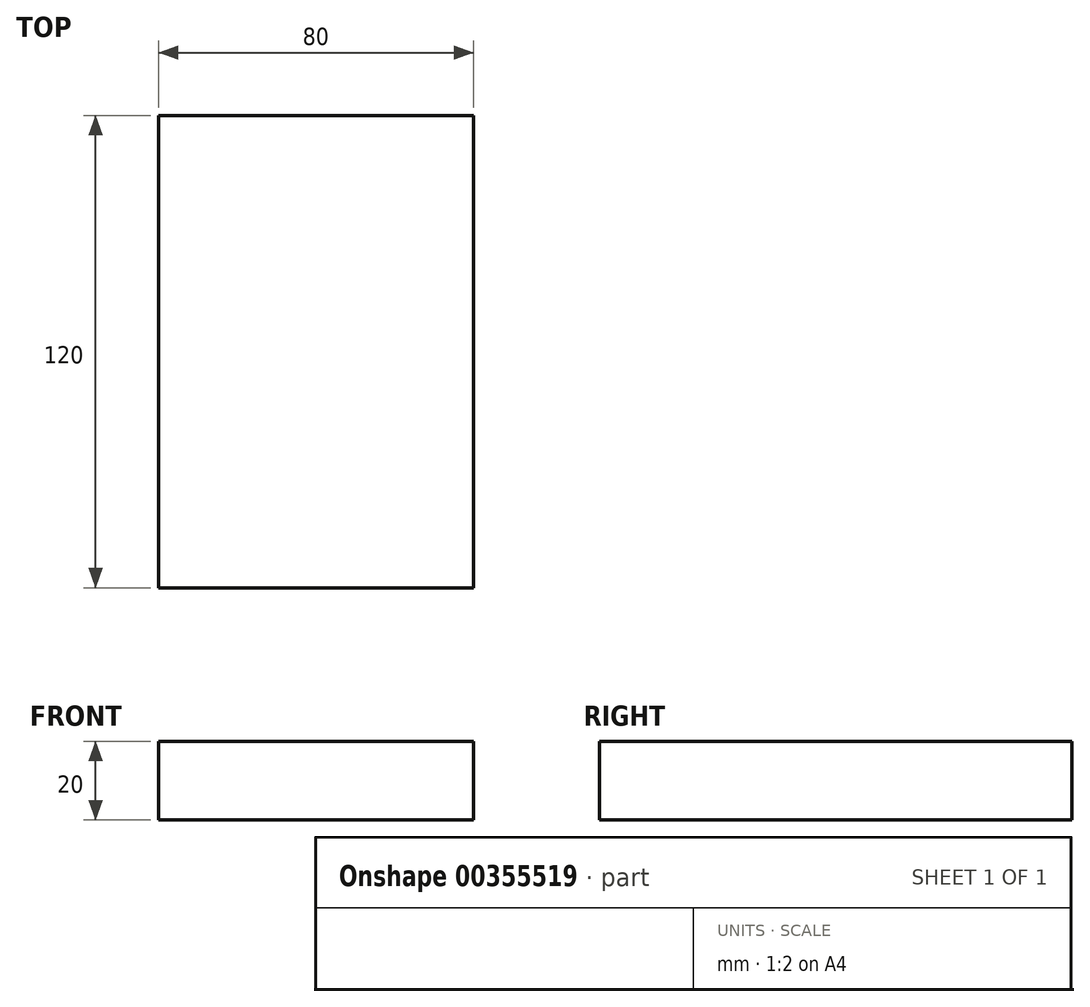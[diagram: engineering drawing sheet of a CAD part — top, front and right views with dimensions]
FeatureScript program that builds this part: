
annotation { "Feature Type Name" : "Feature", "Feature Type Description" : "" }
export const myFeature = defineFeature(function(context is Context, id is Id, definition is map)
    precondition{}
    {
        {
            var Q0;
            Q0=qCreatedBy(makeId("Front.planeOp"),FACE);
            var sketch = newSketch(context, id + "F0", { "sketchPlane" : qUnion([Q0])});
            skLineSegment(sketch, "E0.bottom", {"start": v(40, 10) * mm, "end": v(-40, 10) * mm});
            skLineSegment(sketch, "E0.top", {"start": v(40, -10) * mm, "end": v(-40, -10) * mm});
            skLineSegment(sketch, "E0.left", {"start": v(40, 10) * mm, "end": v(40, -10) * mm});
            skLineSegment(sketch, "E0.right", {"start": v(-40, 10) * mm, "end": v(-40, -10) * mm});
            skPoint(sketch, "E0.middle", {"position": v(0, 0) * mm});
            skLineSegment(sketch, "E1.bottom", {"start": v(110, 70) * mm, "end": v(60, 70) * mm});
            skLineSegment(sketch, "E1.top", {"start": v(110, 40) * mm, "end": v(60, 40) * mm});
            skLineSegment(sketch, "E1.left", {"start": v(110, 70) * mm, "end": v(110, 40) * mm});
            skLineSegment(sketch, "E1.right", {"start": v(60, 70) * mm, "end": v(60, 40) * mm});
            skPoint(sketch, "E1.middle", {"position": v(85, 55) * mm});
            skLineSegment(sketch, "E2", {"start": v(40, 10) * mm, "end": v(40, 38.08) * mm});
            skArc(sketch, "E3", {"start": v(40, 38.08) * mm, "mid": v(43.51, 46.57) * mm, "end": v(52, 50.08) * mm});
            skLineSegment(sketch, "E4", {"start": v(52, 50.08) * mm, "end": v(85, 50.08) * mm});
            skLineSegment(sketch, "E5.0", {"start": v(52, 62.08) * mm, "end": v(85, 62.08) * mm});
            skArc(sketch, "E5.1", {"start": v(28, 38.08) * mm, "mid": v(35.03, 55.05) * mm, "end": v(52, 62.08) * mm});
            skLineSegment(sketch, "E5.2", {"start": v(28, 10) * mm, "end": v(28, 38.08) * mm});
            skLineSegment(sketch, "E6", {"start": v(85, 70) * mm, "end": v(85, 40) * mm});
            skFitSpline(sketch, "E7", {"points": [v(-40, 10) * mm, v(52, 62.08) * mm], "startDerivative": vector(13.37, 56.52) * mm, "endDerivative": vector(129.8, 3.37) * mm});
            skSolve(sketch);
        }
        {
            var Q0;
            Q0=makeQuery(id+"F0.imprint","IMPRINT",FACE,{"disambiguationData":[TD([[makeQuery(id+"F0.imprint","IMPRINT",EDGE,{"derivedFrom":sQuery(id+"F0.wireOp",EDGE,"E0.top")}),-1.0]])]});
            extrude(context, id + "F1", {"entities" : qUnion([Q0]), "endBound" : BoundingType.SYMMETRIC, "depth" : 120 * mm});
        }
    });
